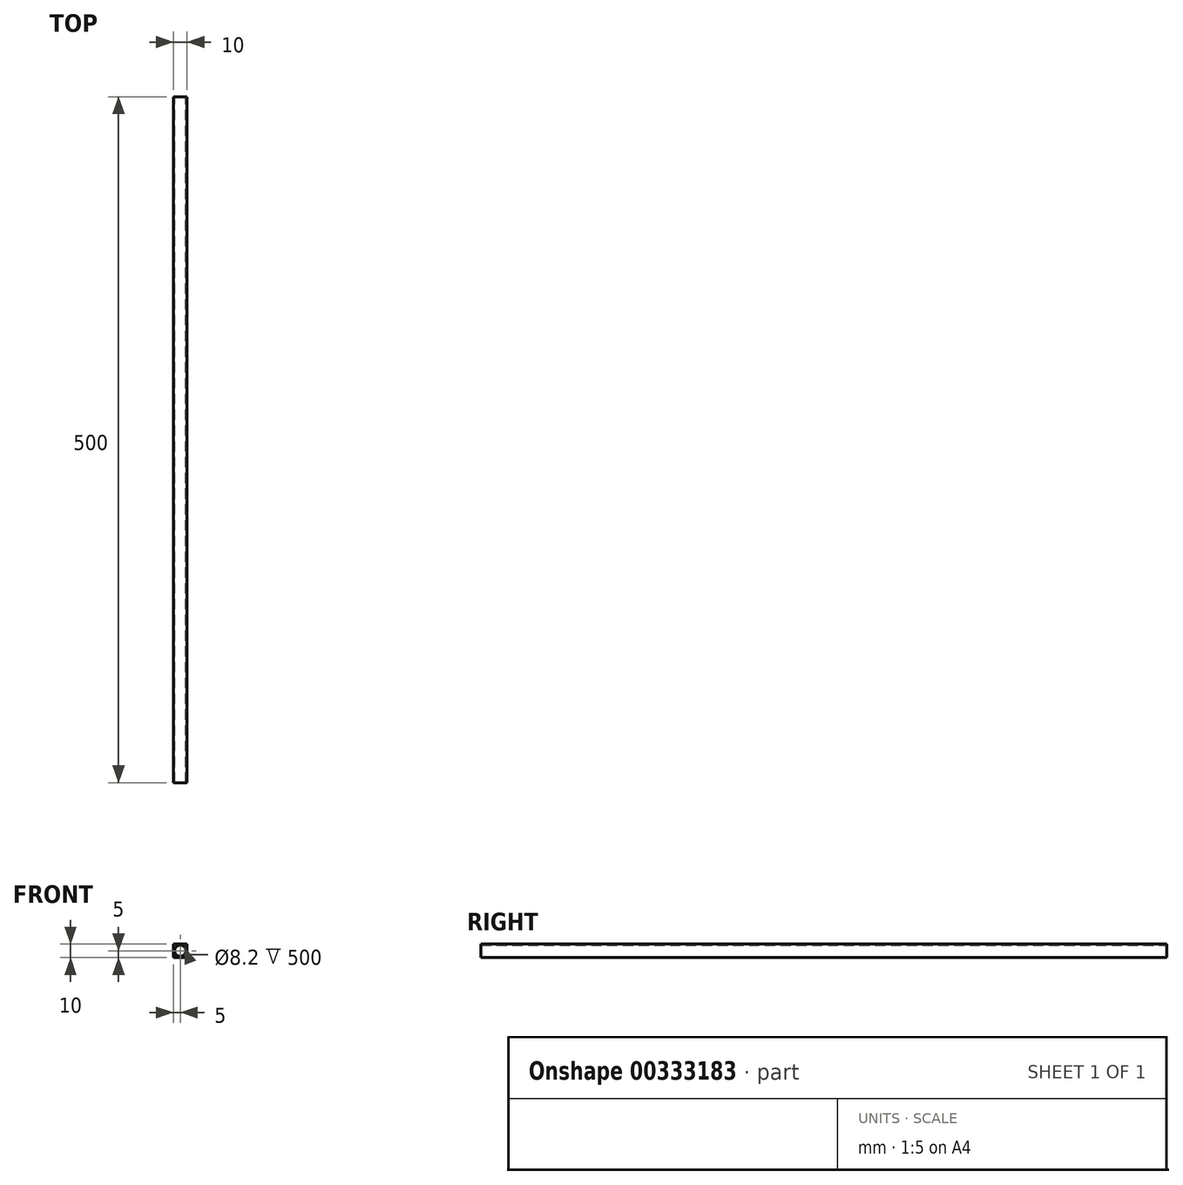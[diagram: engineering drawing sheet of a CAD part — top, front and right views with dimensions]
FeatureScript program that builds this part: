
annotation { "Feature Type Name" : "Feature", "Feature Type Description" : "" }
export const myFeature = defineFeature(function(context is Context, id is Id, definition is map)
    precondition{}
    {
        {
            var Q0;
            Q0=qCreatedBy(makeId("Front.planeOp"),FACE);
            var sketch = newSketch(context, id + "F0", { "sketchPlane" : qUnion([Q0])});
            skLineSegment(sketch, "E0.bottom", {"start": v(5, -5) * mm, "end": v(-5, -5) * mm});
            skLineSegment(sketch, "E0.top", {"start": v(5, 5) * mm, "end": v(-5, 5) * mm});
            skLineSegment(sketch, "E0.left", {"start": v(5, -5) * mm, "end": v(5, 5) * mm});
            skLineSegment(sketch, "E0.right", {"start": v(-5, -5) * mm, "end": v(-5, 5) * mm});
            skPoint(sketch, "E0.middle", {"position": v(0, 0) * mm});
            skCircle(sketch, "E1", {"center": v(0, 0) * mm, "radius": 4.1 * mm});
            skSolve(sketch);
        }
        {
            var Q0;
            Q0=qSketchRegion(id+"F0",true);
            extrude(context, id + "F1", {"entities" : qUnion([Q0]), "depth" : 500 * mm});
        }
    });
